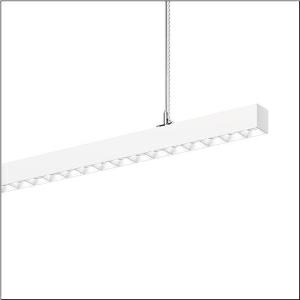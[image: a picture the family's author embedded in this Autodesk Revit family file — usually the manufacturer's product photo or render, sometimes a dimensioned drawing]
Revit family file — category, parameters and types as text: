
# Revit family: silica_r__21_51mx36da47wb_ab97
name_source: partatom
category: Lighting Fixtures
units: mm (PartAtom-declared; Revit-internal decimal feet)

## family parameters
Cut with Voids When Loaded = No
Host = Face
Light Source = No
Part Type = Normal
Room Calculation Point = No
Round Connector Dimension = Use Diameter
Shared = No

## types (1)
- --- (1 x LED, 7060 lm, 40.3 W, 4000K)
    Apparent Load = 40 VA
    CIE Flux Codes = 83 98 100 61 100
    Color Rendering = 80
    Color Temperature = 4000K
    Default Elevation = 1800 mm
    Description = Silica® 21, office luminaire, primary light control with darklight reflector, of PMMA, white, CAT 2 (L<= 3000cd/m²), light emission: direct/indirect distribution, primary light characteristic: symmetric, installation type: suspended mounting, LED, rated luminous flux: 7.060lm, luminous efficacy: 175lm/W, light colour: 840, colour temperature: 4000K, with terminal, 3+2-pole, max. 2.5mm², mains connection: 220..240V, AC, 50/60Hz, rated input power: 40.3W, luminaire housing, of aluminium, traffic white (RAL 9016), length: 1.204mm, width: 53mm, height: 53mm, protection rating (complete): IP20, insulation class (complete): insulation class I (protective earthing), certification: CE, permissible operating ambient temperature: 0..+35°C, standard: EN 50419, packaging unit: 1 piece
    Height = 53 mm
    Lamp = 1 x LED
    Lamp Light Flux = 7060 lm
    Lamp Power = 40.3 W
    Lamp count = 1
    Length = 1204 mm
    Luminous efficacy = 175 lm/W
    Manufacturer = Siteco
    ModVariant = No
    Model = 51MX36DA47WB
    Mounting Place = Ceiling
    Mounting Type = Pendant
    Number of Poles = 1
    OnlyDefault = Yes
    Power Factor = 1
    Product Name = Silica® 21
    Product group = office luminaire | ceiling pendant
    ProductGroupID = 902
    Protection Class = Protection class I
    Protection Degree = IP 20
    RLX_Detail_Level = 1
    RLX_Emergency_Light_Flux = 0 lm
    RLX_Emergency_Type = 0
    RLX_Emergency_Type_DB = No
    RlxData = <blob elided: 40961 chars, md5=a6d9521c>
    Socket = socket
    Standby Power = 0 W
    System Light Flux = 7060 lm
    System Power = 40 W
    Type Comments = factory setting: luminous flux: 100 % | dim-lin: 254 | 336 mA
    Type Image = l_1297797.jpg
    URL = http://relux.com
    VarID = @adj_052091
    Voltage = 0 V
    Weight = 0.00 kg
    Width = 53 mm

## geometry (parser evidence)
native form markers: Blend x4, Sweep x12
no freeform markers — native parametric forms only
